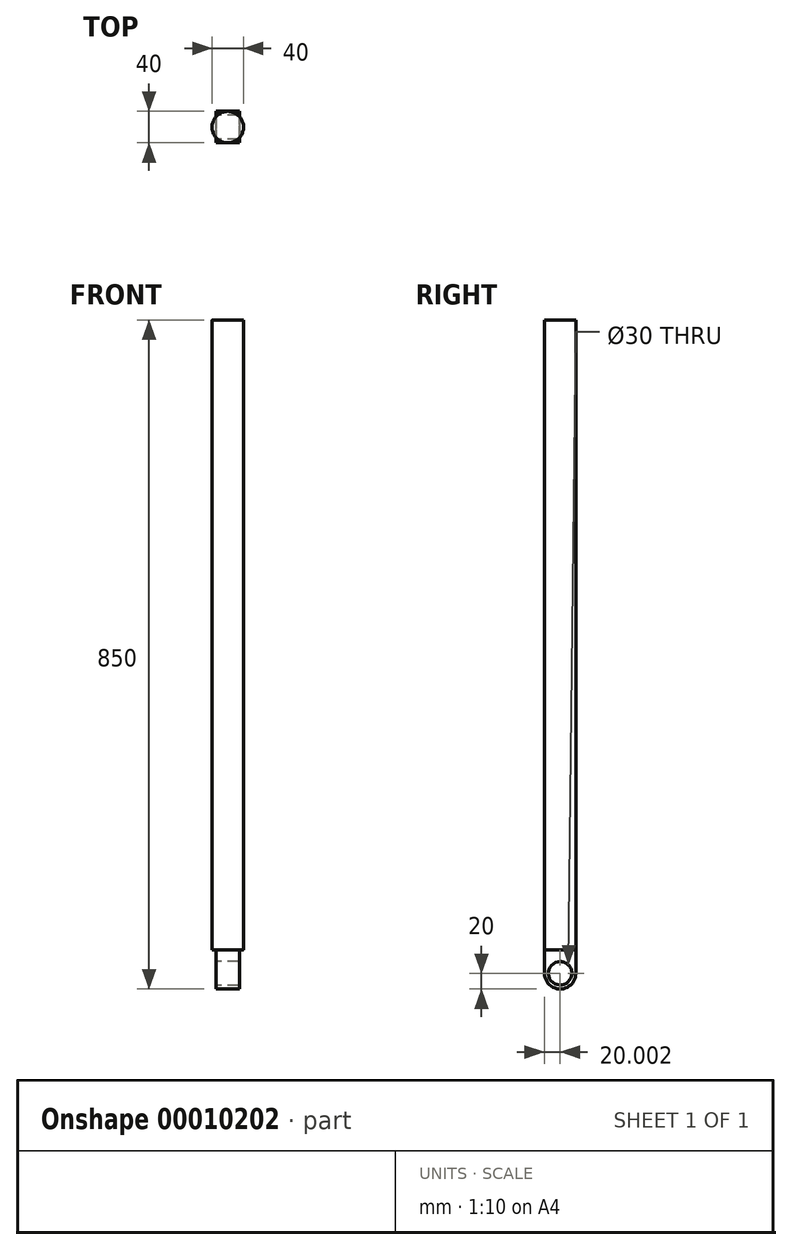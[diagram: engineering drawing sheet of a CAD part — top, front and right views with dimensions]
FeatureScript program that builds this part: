
annotation { "Feature Type Name" : "Feature", "Feature Type Description" : "" }
export const myFeature = defineFeature(function(context is Context, id is Id, definition is map)
    precondition{}
    {
        {
            var Q0;
            Q0=qCreatedBy(makeId("Top.planeOp"),FACE);
            var sketch = newSketch(context, id + "F0", { "sketchPlane" : qUnion([Q0])});
            skCircle(sketch, "E0", {"center": v(0, -12.02) * mm, "radius": 20 * mm});
            skSolve(sketch);
        }
        {
            var Q0;
            Q0=qSketchRegion(id+"F0",true);
            extrude(context, id + "F1", {"entities" : qUnion([Q0]), "depth" : 800 * mm});
        }
        {
            var Q0;
            Q0=makeQuery(id+"F1.opExtrude","CAP_FACE",FACE,{"disambiguationData":[OSD([sQuery(id+"F0.wireOp",EDGE,"E0")])],"isStart":true});
            var sketch = newSketch(context, id + "F2", { "sketchPlane" : qUnion([Q0])});
            skLineSegment(sketch, "E1", {"start": v(0, 12.02) * mm, "end": v(15, 12.02) * mm, "construction": true});
            skLineSegment(sketch, "E2", {"start": v(-15, -7.98) * mm, "end": v(-15, 32.02) * mm});
            skLineSegment(sketch, "E3", {"start": v(-15, 32.02) * mm, "end": v(15, 32.02) * mm});
            skLineSegment(sketch, "E4", {"start": v(-15, -7.98) * mm, "end": v(15, -7.98) * mm});
            skLineSegment(sketch, "E5", {"start": v(15, 32.02) * mm, "end": v(15, -7.98) * mm});
            skSolve(sketch);
        }
        {
            var Q0;
            Q0=qSketchRegion(id+"F2",true);
            extrude(context, id + "F3", {"entities" : qUnion([Q0]), "operationType" : NewBodyOperationType.ADD, "depth" : 50 * mm});
        }
        {
            var Q0;
            Q0=makeQuery(id+"F3.opExtrude","SWEPT_FACE",FACE,{"disambiguationData":[OSD([sQuery(id+"F2.wireOp",EDGE,"E2")])]});
            var sketch = newSketch(context, id + "F4", { "sketchPlane" : qUnion([Q0])});
            skLineSegment(sketch, "E6", {"start": v(12.02, -50) * mm, "end": v(12.02, -30) * mm, "construction": true});
            skArc(sketch, "E7", {"start": v(-7.98, -30) * mm, "mid": v(12.02, -50) * mm, "end": v(32.02, -30) * mm});
            skLineSegment(sketch, "E8", {"start": v(12.02, -50) * mm, "end": v(32.02, -50) * mm});
            skLineSegment(sketch, "E9", {"start": v(32.02, -50) * mm, "end": v(32.02, -30) * mm});
            skLineSegment(sketch, "E10", {"start": v(12.02, -50) * mm, "end": v(-7.98, -50) * mm});
            skLineSegment(sketch, "E11", {"start": v(-7.98, -50) * mm, "end": v(-7.98, -30) * mm});
            skLineSegment(sketch, "E12", {"start": v(32.02, -30) * mm, "end": v(-7.98, -30) * mm, "construction": true});
            skCircle(sketch, "E13", {"center": v(12.02, -30) * mm, "radius": 15 * mm});
            skSolve(sketch);
        }
        {
            var Q0;
            Q0=qSketchRegion(id+"F4",true);
            extrude(context, id + "F5", {"entities" : qUnion([Q0]), "operationType" : NewBodyOperationType.REMOVE, "endBound" : BoundingType.UP_TO_NEXT, "oppositeDirection" : true, "depth" : 25 * mm});
        }
    });
